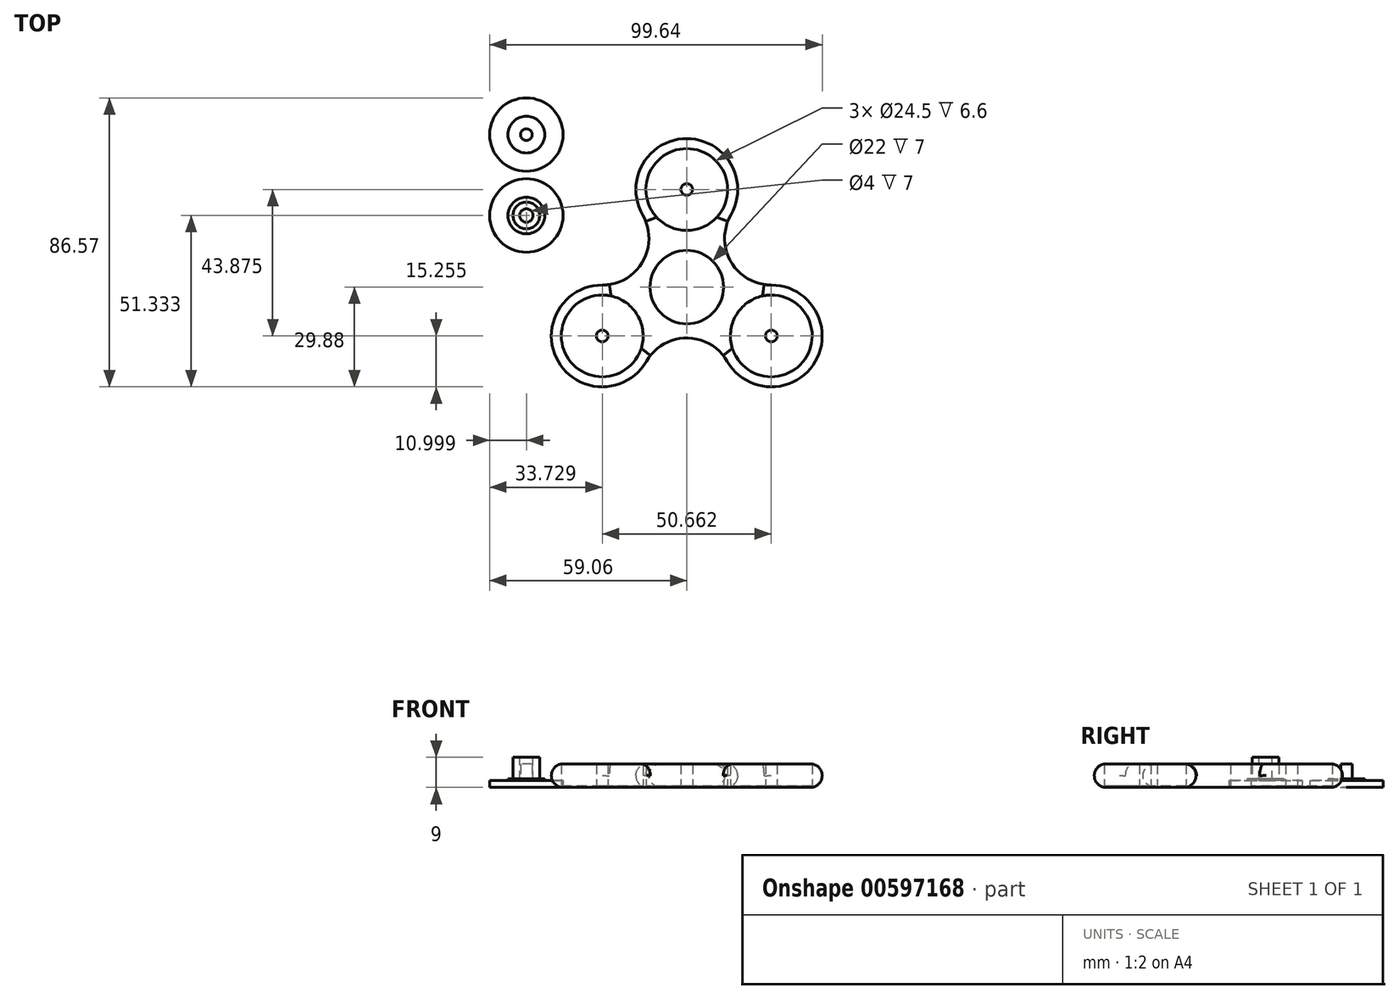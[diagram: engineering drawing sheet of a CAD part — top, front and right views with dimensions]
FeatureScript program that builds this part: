
annotation { "Feature Type Name" : "Feature", "Feature Type Description" : "" }
export const myFeature = defineFeature(function(context is Context, id is Id, definition is map)
    precondition{}
    {
        {
            var Q0;
            Q0=qCreatedBy(makeId("Top.planeOp"),FACE);
            var sketch = newSketch(context, id + "F0", { "sketchPlane" : qUnion([Q0])});
            skCircle(sketch, "E0", {"center": v(0, 0) * mm, "radius": 11 * mm});
            skCircle(sketch, "E1", {"center": v(0, 0) * mm, "radius": 14 * mm});
            skCircle(sketch, "E2", {"center": v(0, 29.25) * mm, "radius": 12.25 * mm});
            skCircle(sketch, "E3", {"center": v(0, 29.25) * mm, "radius": 1.75 * mm});
            skCircle(sketch, "E4", {"center": v(0, 29.25) * mm, "radius": 15.25 * mm});
            skCircle(sketch, "E5.1.0", {"center": v(-25.33, -14.62) * mm, "radius": 15.25 * mm});
            skCircle(sketch, "E5.1.1", {"center": v(-25.33, -14.62) * mm, "radius": 1.75 * mm});
            skCircle(sketch, "E5.1.2", {"center": v(-25.33, -14.62) * mm, "radius": 12.25 * mm});
            skCircle(sketch, "E5.2.0", {"center": v(25.33, -14.62) * mm, "radius": 15.25 * mm});
            skCircle(sketch, "E5.2.1", {"center": v(25.33, -14.62) * mm, "radius": 1.75 * mm});
            skCircle(sketch, "E5.2.2", {"center": v(25.33, -14.62) * mm, "radius": 12.25 * mm});
            skArc(sketch, "E6", {"start": v(-25.33, 0.63) * mm, "mid": v(-13.2, 7.62) * mm, "end": v(-13.2, 21.62) * mm});
            skArc(sketch, "E7.1.0", {"start": v(12.12, -22.25) * mm, "mid": v(0, -15.25) * mm, "end": v(-12.12, -22.25) * mm});
            skArc(sketch, "E7.2.0", {"start": v(13.2, 21.63) * mm, "mid": v(13.2, 7.63) * mm, "end": v(25.33, 0.63) * mm});
            skSolve(sketch);
        }
        {
            var Q0;
            Q0=makeQuery(id+"F0.imprint","IMPRINT",FACE,{"disambiguationData":[TD([[makeQuery(id+"F0.imprint","IMPRINT",EDGE,{"derivedFrom":sQuery(id+"F0.wireOp",EDGE,"E2")}),-1.0]])]});
            var Q1;
            {var subQ5=sQuery(id+"F0.wireOp",EDGE,"E6");Q1=makeQuery(id+"F0.imprint","IMPRINT",FACE,{"disambiguationData":[TD([[makeQuery(id+"F0.imprint","IMPRINT",EDGE,{"derivedFrom":subQ5}),-1.0]])]});}
            var Q2;
            Q2=makeQuery(id+"F0.imprint","IMPRINT",FACE,{"disambiguationData":[TD([[makeQuery(id+"F0.imprint","IMPRINT",EDGE,{"derivedFrom":sQuery(id+"F0.wireOp",EDGE,"E0")}),-1.0]])]});
            var Q3;
            {var subQ5=sQuery(id+"F0.wireOp",EDGE,"E7.2.0");Q3=makeQuery(id+"F0.imprint","IMPRINT",FACE,{"disambiguationData":[TD([[makeQuery(id+"F0.imprint","IMPRINT",EDGE,{"derivedFrom":subQ5}),-1.0]])]});}
            var Q4;
            Q4=makeQuery(id+"F0.imprint","IMPRINT",FACE,{"disambiguationData":[TD([[makeQuery(id+"F0.imprint","IMPRINT",EDGE,{"derivedFrom":sQuery(id+"F0.wireOp",EDGE,"E5.2.2")}),-1.0]])]});
            var Q5;
            {var subQ5=sQuery(id+"F0.wireOp",EDGE,"E7.1.0");Q5=makeQuery(id+"F0.imprint","IMPRINT",FACE,{"disambiguationData":[TD([[makeQuery(id+"F0.imprint","IMPRINT",EDGE,{"derivedFrom":subQ5}),-1.0]])]});}
            var Q6;
            Q6=makeQuery(id+"F0.imprint","IMPRINT",FACE,{"disambiguationData":[TD([[makeQuery(id+"F0.imprint","IMPRINT",EDGE,{"derivedFrom":sQuery(id+"F0.wireOp",EDGE,"E5.1.2")}),-1.0]])]});
            extrude(context, id + "F1", {"entities" : qUnion([Q0, Q1, Q2, Q3, Q4, Q5, Q6]), "depth" : 7 * mm});
        }
        {
            var Q0;
            Q0=makeQuery(id+"F0.imprint","IMPRINT",FACE,{"disambiguationData":[TD([[makeQuery(id+"F0.imprint","IMPRINT",EDGE,{"derivedFrom":sQuery(id+"F0.wireOp",EDGE,"E2")}),1.0]])]});
            var Q1;
            Q1=makeQuery(id+"F0.imprint","IMPRINT",FACE,{"disambiguationData":[TD([[makeQuery(id+"F0.imprint","IMPRINT",EDGE,{"derivedFrom":sQuery(id+"F0.wireOp",EDGE,"E5.1.1")}),-1.0]])]});
            var Q2;
            Q2=makeQuery(id+"F0.imprint","IMPRINT",FACE,{"disambiguationData":[TD([[makeQuery(id+"F0.imprint","IMPRINT",EDGE,{"derivedFrom":sQuery(id+"F0.wireOp",EDGE,"E5.2.1")}),-1.0]])]});
            extrude(context, id + "F2", {"entities" : qUnion([Q0, Q1, Q2]), "operationType" : NewBodyOperationType.ADD, "depth" : 0.4 * mm});
        }
        {
            var Q0;
            Q0=makeQuery(id+"F0.imprint","IMPRINT",FACE,{"disambiguationData":[TD([[makeQuery(id+"F0.imprint","IMPRINT",EDGE,{"derivedFrom":sQuery(id+"F0.wireOp",EDGE,"E3")}),1.0]])]});
            var Q1;
            Q1=makeQuery(id+"F0.imprint","IMPRINT",FACE,{"disambiguationData":[TD([[makeQuery(id+"F0.imprint","IMPRINT",EDGE,{"derivedFrom":sQuery(id+"F0.wireOp",EDGE,"E5.1.1")}),1.0]])]});
            var Q2;
            Q2=makeQuery(id+"F0.imprint","IMPRINT",FACE,{"disambiguationData":[TD([[makeQuery(id+"F0.imprint","IMPRINT",EDGE,{"derivedFrom":sQuery(id+"F0.wireOp",EDGE,"E5.2.1")}),1.0]])]});
            extrude(context, id + "F3", {"entities" : qUnion([Q0, Q1, Q2]), "operationType" : NewBodyOperationType.ADD, "depth" : 7 * mm});
        }
        {
            var Q0;
            Q0=makeQuery(id+"F1.opExtrude","CAP_EDGE",EDGE,{"disambiguationData":[OSD([sQuery(id+"F0.wireOp",EDGE,"E5.1.0")])],"isStart":false});
            var Q1;
            Q1=makeQuery(id+"F1.opExtrude","CAP_EDGE",EDGE,{"disambiguationData":[OSD([sQuery(id+"F0.wireOp",EDGE,"E5.1.0")])],"isStart":true});
            fillet(context, id + "F4", {"entities" : qUnion([Q0, Q1]), "radius" : 3.5 * mm, "tangentPropagation" : true, "allowEdgeOverflow" : false});
        }
        {
            var Q0;
            Q0=qCreatedBy(makeId("Top.planeOp"),FACE);
            var sketch = newSketch(context, id + "F5", { "sketchPlane" : qUnion([Q0])});
            skCircle(sketch, "E8", {"center": v(-48.06, 21.45) * mm, "radius": 11 * mm});
            skCircle(sketch, "E9", {"center": v(-48.06, 45.69) * mm, "radius": 11 * mm});
            skSolve(sketch);
        }
        {
            var Q0;
            Q0=makeQuery(id+"F5.imprint","IMPRINT",FACE,{"disambiguationData":[TD([[makeQuery(id+"F5.imprint","IMPRINT",EDGE,{"derivedFrom":sQuery(id+"F5.wireOp",EDGE,"E8")}),1.0]])]});
            var Q1;
            Q1=makeQuery(id+"F5.imprint","IMPRINT",FACE,{"disambiguationData":[TD([[makeQuery(id+"F5.imprint","IMPRINT",EDGE,{"derivedFrom":sQuery(id+"F5.wireOp",EDGE,"E9")}),1.0]])]});
            extrude(context, id + "F6", {"entities" : qUnion([Q0, Q1]), "depth" : 2 * mm});
        }
        {
            var Q0;
            Q0=makeQuery(id+"F6.opExtrude","CAP_FACE",FACE,{"disambiguationData":[OSD([sQuery(id+"F5.wireOp",EDGE,"E8")])],"isStart":false});
            var sketch = newSketch(context, id + "F7", { "sketchPlane" : qUnion([Q0])});
            skCircle(sketch, "E10", {"center": v(-48.06, 21.45) * mm, "radius": 4 * mm});
            skSolve(sketch);
        }
        {
            var Q0;
            Q0=makeQuery(id+"F7.imprint","IMPRINT",FACE,{"disambiguationData":[TD([[makeQuery(id+"F7.imprint","IMPRINT",EDGE,{"derivedFrom":sQuery(id+"F7.wireOp",EDGE,"E10")}),1.0]])]});
            extrude(context, id + "F8", {"entities" : qUnion([Q0]), "operationType" : NewBodyOperationType.ADD, "depth" : 7 * mm});
        }
        {
            var Q0;
            Q0=makeQuery(id+"F8.opExtrude","CAP_FACE",FACE,{"disambiguationData":[OSD([sQuery(id+"F7.wireOp",EDGE,"E10")])],"isStart":false});
            var sketch = newSketch(context, id + "F9", { "sketchPlane" : qUnion([Q0])});
            skCircle(sketch, "E11", {"center": v(-48.06, 21.45) * mm, "radius": 2 * mm});
            skSolve(sketch);
        }
        {
            var Q0;
            Q0=makeQuery(id+"F9.imprint","IMPRINT",FACE,{"disambiguationData":[TD([[makeQuery(id+"F9.imprint","IMPRINT",EDGE,{"derivedFrom":sQuery(id+"F9.wireOp",EDGE,"E11")}),1.0]])]});
            extrude(context, id + "F10", {"entities" : qUnion([Q0]), "operationType" : NewBodyOperationType.REMOVE, "oppositeDirection" : true, "depth" : 7 * mm});
        }
        {
            var Q0;
            Q0=makeQuery(id+"F6.opExtrude","CAP_FACE",FACE,{"disambiguationData":[OSD([sQuery(id+"F5.wireOp",EDGE,"E9")])],"isStart":false});
            var sketch = newSketch(context, id + "F11", { "sketchPlane" : qUnion([Q0])});
            skCircle(sketch, "E12", {"center": v(-48.06, 45.69) * mm, "radius": 1.75 * mm});
            skSolve(sketch);
        }
        {
            var Q0;
            Q0=qSketchRegion(id+"F11",true);
            extrude(context, id + "F12", {"entities" : qUnion([Q0]), "operationType" : NewBodyOperationType.ADD, "depth" : 5 * mm});
        }
        {
            var Q0;
            Q0=makeQuery(id+"F6.opExtrude","CAP_FACE",FACE,{"disambiguationData":[OSD([sQuery(id+"F5.wireOp",EDGE,"E8")])],"isStart":false});
            var sketch = newSketch(context, id + "F13", { "sketchPlane" : qUnion([Q0])});
            skCircle(sketch, "E13", {"center": v(-48.06, 21.45) * mm, "radius": 5.5 * mm});
            skCircle(sketch, "E14", {"center": v(-48.06, 45.69) * mm, "radius": 5.5 * mm});
            skSolve(sketch);
        }
        {
            var Q0;
            Q0=makeQuery(id+"F13.imprint","IMPRINT",FACE,{"disambiguationData":[TD([[makeQuery(id+"F13.imprint","IMPRINT",EDGE,{"derivedFrom":sQuery(id+"F13.wireOp",EDGE,"E14")}),1.0]])]});
            var Q1;
            Q1=makeQuery(id+"F13.imprint","IMPRINT",FACE,{"disambiguationData":[TD([[makeQuery(id+"F13.imprint","IMPRINT",EDGE,{"derivedFrom":sQuery(id+"F13.wireOp",EDGE,"E13")}),1.0]])]});
            extrude(context, id + "F14", {"entities" : qUnion([Q0, Q1]), "operationType" : NewBodyOperationType.ADD, "depth" : 0.5 * mm});
        }
    });
